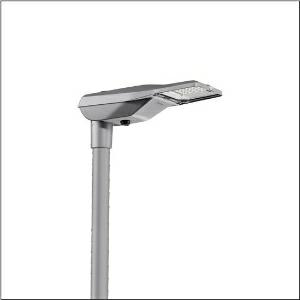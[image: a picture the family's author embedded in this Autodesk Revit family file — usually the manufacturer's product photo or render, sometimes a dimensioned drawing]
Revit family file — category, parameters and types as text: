
# Revit family: streetlight_sl_21_iq_micro___p0_8ab_5xe1r31u08cb_a822
name_source: partatom
category: Lighting Fixtures
units: mm (PartAtom-declared; Revit-internal decimal feet)

## family parameters
Cut with Voids When Loaded = No
Host = Face
Light Source = No
Part Type = Normal
Room Calculation Point = No
Round Connector Dimension = Use Diameter
Shared = No

## types (1)
- --- (1 x LED, 2570 lm, 19.1 W, 3000K)
    Apparent Load = 19 VA
    CIE Flux Codes = 36 71 98 100 100
    Color Rendering = 70
    Color Temperature = 3000K
    Default Elevation = 1800 mm
    Description = Streetlight SL 21 iQ micro, mast luminaire, primary light control with lens, of PMMA, primary optical cover: cover, of toughened safety glass, transparent, light distribution: P0.8aB, light emission: direct distribution, primary light characteristic: asymmetric, installation type: post-top, side-entry, LED, High Power LED, rated luminous flux: 2.570lm, luminous efficacy: 135lm/W, light colour: 730, colour temperature: 3000K, control gear: iQ-Street Remote, D4i with power reduction, control: pre-setting: logarithmic dimming characteristic, Street-Remote, Auto-Match, Temp-Guard, Lumen-Switch, Night-Set, Smart-Wire, Light-Fading, Desk-Remote (wireless, voltage-free reading and setting of iQ features in the workshop via application-optimized NFC function/RFID function), optimised constant luminous flux control (CLO 2.0), mains connection: 220..240V, AC, 50/60Hz, start of lifetime: 19W, end of service life: 20W, reduction: 9W, luminaire housing, of diecast aluminium, powder-coated, SITECO metallic grey (DB 702S), corrosivity category C5 high according to DIN EN ISO 12944, please order mast flange separately, inclination adjustable: 0°, 5°, 10°, 15°, sealing non-destructively replaceable, multi-level sealing system, length: 528mm, width: 235mm, height: 110mm, mast flange for spigot size: 42mm (side-entry): 5XC10008XM4, 60/48mm (side-entry/post-top): 5XC10108XM2, 76/60mm (side-entry/post-top): 5XC10108XM1, mounting height: 4..8m, Smart Interface below, protection rating (complete): IP66, insulation class (complete): insulation class II (safety insulation), certification: CE, ENEC, ENEC+, VDE, impact resistance: IK10, permissible operating ambient temperature for outdoor applications: -40..+50°C, standard-compliant lighting for roads and squares, packaging unit: 1 piece

Light Distribution: P0.8aB
    Height = 110 mm
    Lamp = 1 x LED
    Lamp Light Flux = 2570 lm
    Lamp Power = 19.1 W
    Lamp count = 1
    Length = 528 mm
    Luminous efficacy = 135 lm/W
    Manufacturer = Siteco
    ModVariant = No
    Model = 5XE1R31U08CB
    Number of Poles = 1
    OnlyDefault = Yes
    Power Factor = 1
    Product Name = Streetlight SL 21 iQ micro | P0.8aB
    Product group = mast luminaire | pylon top
    ProductGroupID = 6100
    Protection Class = Protection class II
    Protection Degree = IP 66
    RLX_Detail_Level = 1
    RLX_Emergency_Light_Flux = 0 lm
    RLX_Emergency_Type = 0
    RLX_Emergency_Type_DB = No
    RlxData = <blob elided: 99517 chars, md5=f2408a93>
    Socket = socket
    Standby Power = 0 W
    System Light Flux = 2570 lm
    System Power = 19 W
    Type Comments = factory setting: luminous flux: 100 % | dim-lin: 254 | 387 mA
    Type Image = l_1277290.jpg
    URL = http://relux.com
    VarID = @adj_083475
    Voltage = 0 V
    Weight = 0.00 kg
    Width = 235 mm

## geometry (parser evidence)
native form markers: Blend x4, Sweep x9
no freeform markers — native parametric forms only
